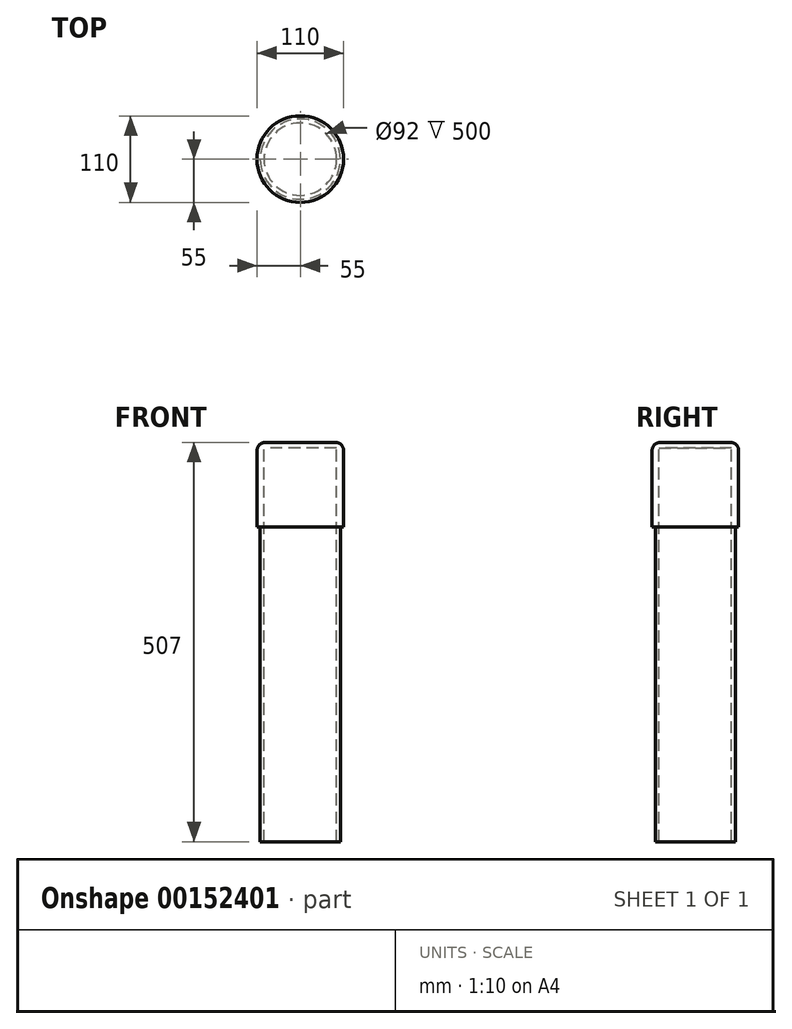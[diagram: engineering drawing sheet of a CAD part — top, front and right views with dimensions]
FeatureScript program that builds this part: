
annotation { "Feature Type Name" : "Feature", "Feature Type Description" : "" }
export const myFeature = defineFeature(function(context is Context, id is Id, definition is map)
    precondition{}
    {
        {
            var Q0;
            Q0=qCreatedBy(makeId("Top.planeOp"),FACE);
            var sketch = newSketch(context, id + "F0", { "sketchPlane" : qUnion([Q0])});
            skCircle(sketch, "E0", {"center": v(0, 0) * mm, "radius": 55 * mm});
            skCircle(sketch, "E1", {"center": v(0, 0) * mm, "radius": 51 * mm});
            skCircle(sketch, "E2", {"center": v(0, 0) * mm, "radius": 46 * mm});
            skSolve(sketch);
        }
        {
            var Q0;
            Q0=makeQuery(id+"F0.imprint","IMPRINT",FACE,{"disambiguationData":[TD([[makeQuery(id+"F0.imprint","IMPRINT",EDGE,{"derivedFrom":sQuery(id+"F0.wireOp",EDGE,"E0")}),1.0]])]});
            var Q1;
            Q1=makeQuery(id+"F0.imprint","IMPRINT",FACE,{"disambiguationData":[TD([[makeQuery(id+"F0.imprint","IMPRINT",EDGE,{"derivedFrom":sQuery(id+"F0.wireOp",EDGE,"E1")}),1.0]])]});
            var Q2;
            Q2=makeQuery(id+"F0.imprint","IMPRINT",FACE,{"disambiguationData":[TD([[makeQuery(id+"F0.imprint","IMPRINT",EDGE,{"derivedFrom":sQuery(id+"F0.wireOp",EDGE,"E2")}),1.0]])]});
            extrude(context, id + "F1", {"entities" : qUnion([Q0, Q1, Q2]), "depth" : 7 * mm});
        }
        {
            var Q0;
            Q0=makeQuery(id+"F0.imprint","IMPRINT",FACE,{"disambiguationData":[TD([[makeQuery(id+"F0.imprint","IMPRINT",EDGE,{"derivedFrom":sQuery(id+"F0.wireOp",EDGE,"E1")}),1.0]])]});
            extrude(context, id + "F2", {"entities" : qUnion([Q0]), "operationType" : NewBodyOperationType.ADD, "oppositeDirection" : true, "depth" : 500 * mm});
        }
        {
            var Q0;
            Q0 = qSketchRegion(id + "F0", true);
            extrude(context, id + "F3", {"entities" : qUnion([Q0]), "operationType" : NewBodyOperationType.ADD, "oppositeDirection" : true, "depth" : 100 * mm});
        }
        {
            var Q0;
            Q0=makeQuery(id+"F1.opExtrude","CAP_EDGE",EDGE,{"disambiguationData":[OSD([sQuery(id+"F0.wireOp",EDGE,"E0")])],"isStart":false});
            fillet(context, id + "F4", {"entities" : qUnion([Q0]), "radius" : 10 * mm, "tangentPropagation" : true, "allowEdgeOverflow" : false});
        }
    });
